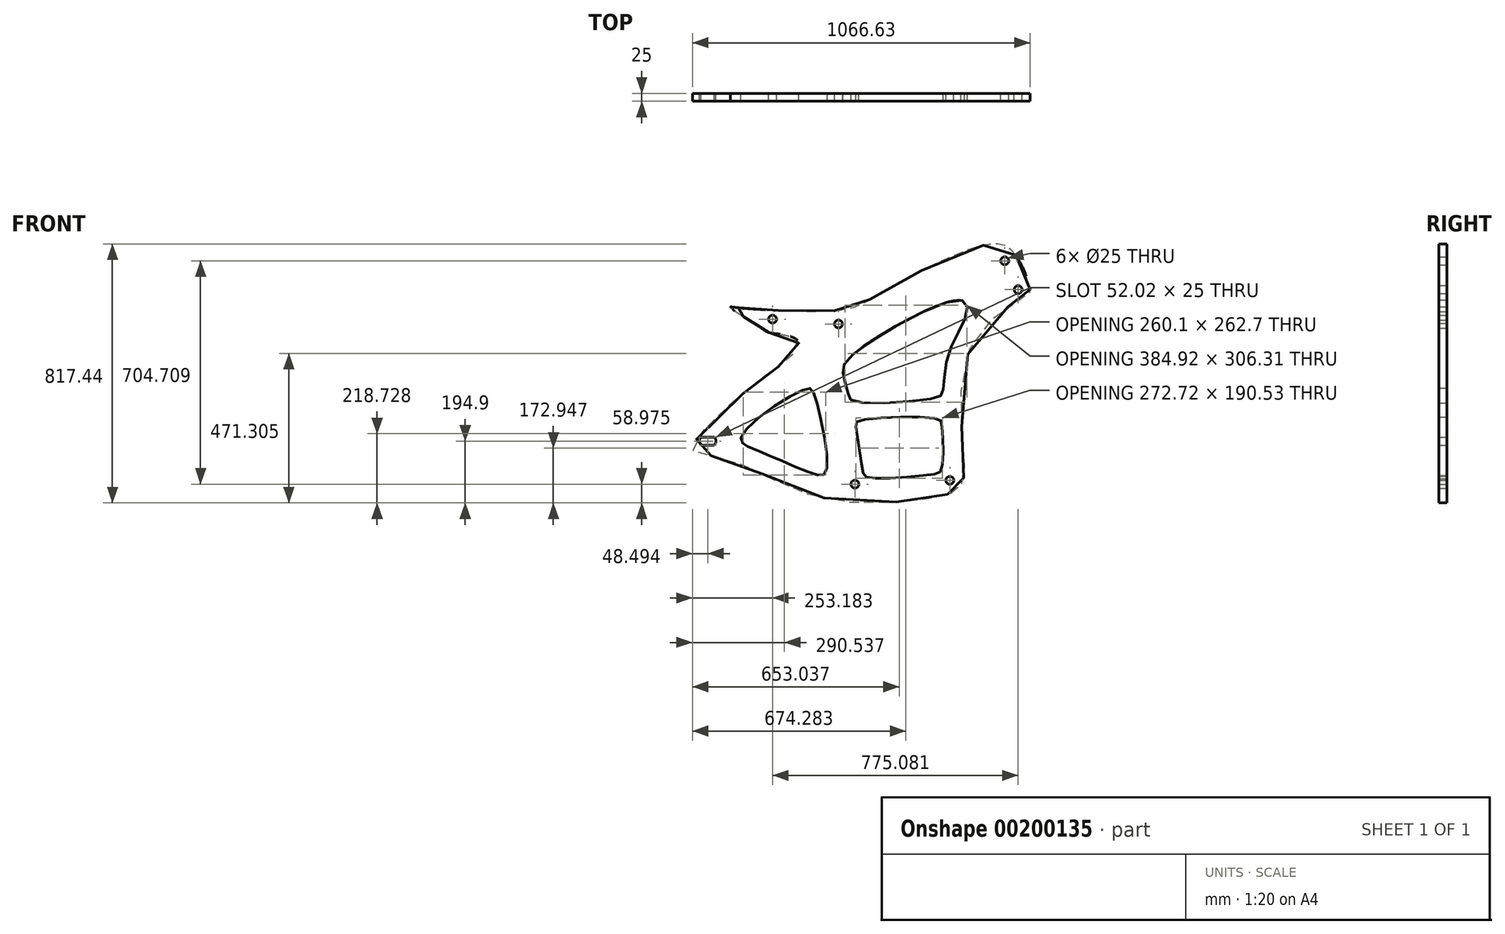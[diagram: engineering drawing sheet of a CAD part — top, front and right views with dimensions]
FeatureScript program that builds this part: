
annotation { "Feature Type Name" : "Feature", "Feature Type Description" : "" }
export const myFeature = defineFeature(function(context is Context, id is Id, definition is map)
    precondition{}
    {
        {
            var Q0;
            Q0=qCreatedBy(makeId("Front.planeOp"),FACE);
            var sketch = newSketch(context, id + "F0", { "sketchPlane" : qUnion([Q0])});
            skLineSegment(sketch, "E0", {"start": v(-1543.48, 0) * mm, "end": v(0, 0) * mm});
            skCircle(sketch, "E1", {"center": v(-1153.7, 325) * mm, "radius": 325 * mm});
            skLineSegment(sketch, "E2", {"start": v(-1464.32, 991.14) * mm, "end": v(-1407.27, 868.78) * mm});
            skLineSegment(sketch, "E3", {"start": v(-1352.33, 750.96) * mm, "end": v(-1002.15, 0) * mm});
            skLineSegment(sketch, "E4", {"start": v(-1365, 778.15) * mm, "end": v(-1352.33, 750.96) * mm});
            skLineSegment(sketch, "E5", {"start": v(-1407.27, 868.78) * mm, "end": v(-1365, 778.15) * mm});
            skPoint(sketch, "E6.orphan", {"position": v(-1449.53, 959.42) * mm});
            skCircle(sketch, "E7", {"center": v(-1195.96, 415.63) * mm, "radius": 325 * mm});
            skLineSegment(sketch, "E8", {"start": v(-1543.48, 0) * mm, "end": v(-2319.15, 0) * mm});
            skLineSegment(sketch, "E9", {"start": v(-1518.45, 1000) * mm, "end": v(-1518.45, 730) * mm});
            skLineSegment(sketch, "E10", {"start": v(-1518.45, 730) * mm, "end": v(-1888.45, 730) * mm});
            skLineSegment(sketch, "E11", {"start": v(-1888.45, 730) * mm, "end": v(-2038.45, 730) * mm});
            skLineSegment(sketch, "E12", {"start": v(-2038.45, 730) * mm, "end": v(-2238.45, 730) * mm});
            skLineSegment(sketch, "E13", {"start": v(-2038.45, 730) * mm, "end": v(-2038.45, 130) * mm});
            skLineSegment(sketch, "E14", {"start": v(-2038.45, 130) * mm, "end": v(-2038.45, 0) * mm});
            skLineSegment(sketch, "E15", {"start": v(-2038.45, 730) * mm, "end": v(-1518.45, 1000) * mm});
            skLineSegment(sketch, "E16", {"start": v(-2432.31, 130) * mm, "end": v(-1461.35, 130) * mm, "construction": true});
            skLineSegment(sketch, "E17", {"start": v(-2319.15, 0) * mm, "end": v(-2766.3, 0) * mm});
            skCircle(sketch, "E18", {"center": v(-2344.78, 300) * mm, "radius": 300 * mm});
            skLineSegment(sketch, "E19", {"start": v(-2344.78, 300) * mm, "end": v(-2014.78, 300) * mm});
            skLineSegment(sketch, "E20", {"start": v(-2014.78, 300) * mm, "end": v(-1564.78, 300) * mm});
            skLineSegment(sketch, "E21", {"start": v(-1564.78, 300) * mm, "end": v(-1164.78, 300) * mm});
            skSolve(sketch);
        }
        {
            var Q0;
            Q0=qCreatedBy(makeId("Front.planeOp"),FACE);
            var sketch = newSketch(context, id + "F1", { "sketchPlane" : qUnion([Q0])});
            skFitSpline(sketch, "E22", {"points": [v(-1372, 886.45) * mm, v(-1461.07, 920.35) * mm, v(-1799.68, 766.44) * mm, v(-1912.44, 715.01) * mm, v(-2161.17, 714.16) * mm, v(-2261.46, 722.42) * mm, v(-2273.57, 722.01) * mm, v(-2170.05, 653.08) * mm, v(-2152.94, 642.81) * mm, v(-2059.2, 616) * mm, v(-2099.76, 552.23) * mm, v(-2190.88, 484.13) * mm, v(-2393.27, 276.94) * mm, v(-2296.94, 246.73) * mm, v(-1987.56, 122.25) * mm, v(-1614.13, 125.88) * mm, v(-1550.76, 153.03) * mm, v(-1534.5, 220.1) * mm, v(-1509.34, 606.92) * mm, v(-1333.48, 762.78) * mm, v(-1327.08, 778.15) * mm, v(-1372, 886.45) * mm]});
            skFitSpline(sketch, "E23", {"points": [v(-2182.09, 268.1) * mm, v(-2220.78, 284.02) * mm, v(-2239.47, 312.76) * mm, v(-2035.39, 465.1) * mm, v(-2008.08, 446.42) * mm, v(-1970.64, 204.43) * mm, v(-2011.73, 197.18) * mm, v(-2182.09, 268.1) * mm]});
            skFitSpline(sketch, "E24", {"points": [v(-1887.8, 572.48) * mm, v(-1917.65, 515.68) * mm, v(-1900.74, 447) * mm, v(-1883.97, 426.03) * mm, v(-1624, 437.21) * mm, v(-1601.65, 458.18) * mm, v(-1585.4, 572.48) * mm, v(-1527.46, 702.85) * mm, v(-1545.57, 744.5) * mm, v(-1887.8, 572.48) * mm]});
            skCircle(sketch, "E25", {"center": v(-2140.09, 684.73) * mm, "radius": 12.5 * mm});
            skCircle(sketch, "E26", {"center": v(-2140.09, 684.73) * mm, "radius": 7.5 * mm});
            skCircle(sketch, "E27", {"center": v(-1407.27, 868.78) * mm, "radius": 12.5 * mm});
            skCircle(sketch, "E28", {"center": v(-1407.27, 868.78) * mm, "radius": 7.5 * mm});
            skCircle(sketch, "E29", {"center": v(-1365, 778.15) * mm, "radius": 12.5 * mm});
            skCircle(sketch, "E30", {"center": v(-1365, 778.15) * mm, "radius": 7.5 * mm});
            skCircle(sketch, "E31", {"center": v(-1580.45, 176.2) * mm, "radius": 12.5 * mm});
            skCircle(sketch, "E32", {"center": v(-1580.45, 176.2) * mm, "radius": 7.5 * mm});
            skCircle(sketch, "E33", {"center": v(-1880.2, 164.08) * mm, "radius": 12.5 * mm});
            skCircle(sketch, "E34", {"center": v(-1880.2, 164.08) * mm, "radius": 7.5 * mm});
            skCircle(sketch, "E35", {"center": v(-1931.99, 669.4) * mm, "radius": 12.5 * mm});
            skCircle(sketch, "E36", {"center": v(-1931.99, 669.4) * mm, "radius": 7.5 * mm});
            skFitSpline(sketch, "E37", {"points": [v(-1876.6, 345.72) * mm, v(-1868.22, 364.56) * mm, v(-1621.11, 370.85) * mm, v(-1605.84, 350.56) * mm, v(-1605.84, 213.6) * mm, v(-1637.87, 194.94) * mm, v(-1836.45, 184.24) * mm, v(-1855.65, 207.5) * mm, v(-1876.6, 345.72) * mm]});
            skLineSegment(sketch, "E38.bottom", {"start": v(-2329.78, 295) * mm, "end": v(-2359.78, 295) * mm});
            skLineSegment(sketch, "E38.top", {"start": v(-2329.78, 305) * mm, "end": v(-2359.78, 305) * mm});
            skLineSegment(sketch, "E38.left", {"start": v(-2329.78, 295) * mm, "end": v(-2329.78, 305) * mm});
            skLineSegment(sketch, "E38.right", {"start": v(-2359.78, 295) * mm, "end": v(-2359.78, 305) * mm});
            skPoint(sketch, "E38.middle", {"position": v(-2344.78, 300) * mm});
            skLineSegment(sketch, "E39.0", {"start": v(-2324.78, 310) * mm, "end": v(-2364.78, 310) * mm});
            skLineSegment(sketch, "E39.1", {"start": v(-2324.78, 290) * mm, "end": v(-2324.78, 310) * mm});
            skLineSegment(sketch, "E39.2", {"start": v(-2324.78, 290) * mm, "end": v(-2364.78, 290) * mm});
            skLineSegment(sketch, "E39.3", {"start": v(-2364.78, 290) * mm, "end": v(-2364.78, 310) * mm});
            skArc(sketch, "E40", {"start": v(-2364.78, 310) * mm, "mid": v(-2368.29, 300) * mm, "end": v(-2364.78, 290) * mm});
            skArc(sketch, "E41.MirrorCS", {"start": v(-2324.78, 310) * mm, "mid": v(-2321.27, 300) * mm, "end": v(-2324.78, 290) * mm});
            skLineSegment(sketch, "E42.0", {"start": v(-2323.63, 312.5) * mm, "end": v(-2365.92, 312.5) * mm});
            skArc(sketch, "E42.1", {"start": v(-2323.63, 312.5) * mm, "mid": v(-2318.77, 300) * mm, "end": v(-2323.63, 287.5) * mm});
            skLineSegment(sketch, "E42.2", {"start": v(-2323.63, 287.5) * mm, "end": v(-2365.92, 287.5) * mm});
            skArc(sketch, "E42.3", {"start": v(-2365.92, 312.5) * mm, "mid": v(-2370.79, 300) * mm, "end": v(-2365.92, 287.5) * mm});
            skSolve(sketch);
        }
        {
            var Q0;
            Q0=makeQuery(id+"F1.imprint","IMPRINT",FACE,{"disambiguationData":[TD([[makeQuery(id+"F1.imprint","IMPRINT",EDGE,{"derivedFrom":sQuery(id+"F1.wireOp",EDGE,"E22")}),1.0]])]});
            extrude(context, id + "F2", {"entities" : qUnion([Q0]), "depth" : 25 * mm});
        }
    });
